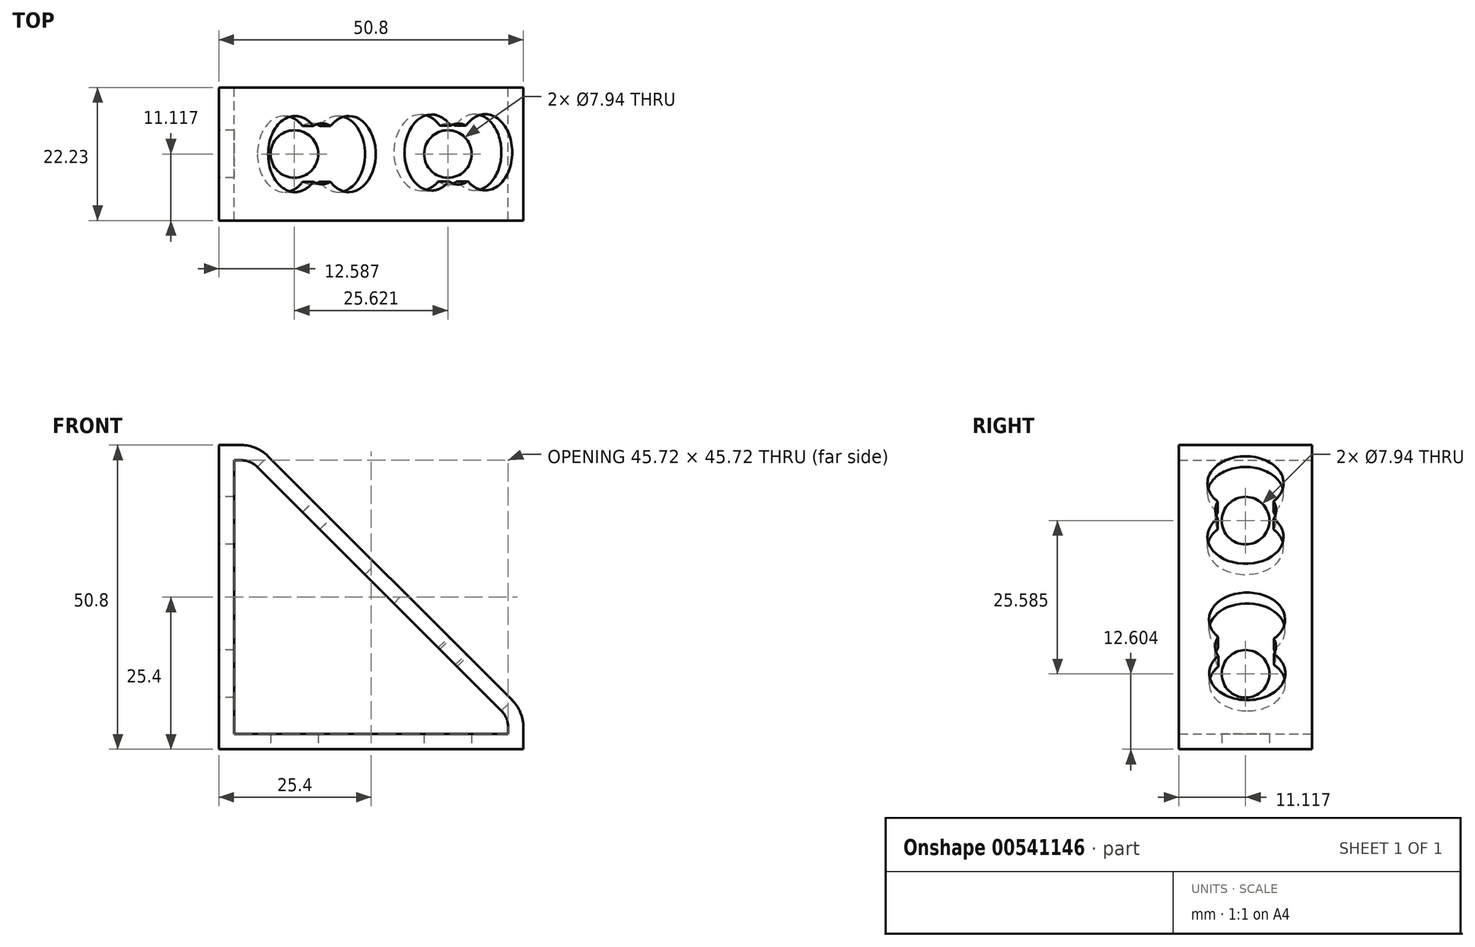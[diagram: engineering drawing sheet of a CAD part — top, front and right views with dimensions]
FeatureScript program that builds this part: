
annotation { "Feature Type Name" : "Feature", "Feature Type Description" : "" }
export const myFeature = defineFeature(function(context is Context, id is Id, definition is map)
    precondition{}
    {
        {
            var Q0;
            Q0=qCreatedBy(makeId("Front.planeOp"),FACE);
            var sketch = newSketch(context, id + "F0", { "sketchPlane" : qUnion([Q0])});
            skLineSegment(sketch, "E0", {"start": v(0, 0) * mm, "end": v(50.8, 0) * mm});
            skLineSegment(sketch, "E1", {"start": v(0, 0) * mm, "end": v(0, 50.8) * mm});
            skLineSegment(sketch, "E2", {"start": v(0, 50.8) * mm, "end": v(3.72, 50.8) * mm});
            skLineSegment(sketch, "E3", {"start": v(50.8, 0) * mm, "end": v(50.8, 3.72) * mm});
            skLineSegment(sketch, "E4", {"start": v(8.2, 48.94) * mm, "end": v(48.94, 8.2) * mm});
            skPoint(sketch, "E5.visualSharp", {"position": v(6.35, 50.8) * mm});
            skArc(sketch, "E5.filletArc", {"start": v(8.2, 48.94) * mm, "mid": v(6.15, 50.32) * mm, "end": v(3.72, 50.8) * mm});
            skPoint(sketch, "E6.visualSharp", {"position": v(50.8, 6.35) * mm});
            skArc(sketch, "E6.filletArc", {"start": v(50.8, 3.72) * mm, "mid": v(50.32, 6.15) * mm, "end": v(48.94, 8.2) * mm});
            skSolve(sketch);
        }
        {
            var Q0;
            Q0=makeQuery(id+"F0.imprint","IMPRINT",FACE,{"disambiguationData":[TD([[makeQuery(id+"F0.imprint","IMPRINT",EDGE,{"derivedFrom":sQuery(id+"F0.wireOp",EDGE,"E0")}),1.0]])]});
            extrude(context, id + "F1", {"entities" : qUnion([Q0]), "depth" : 22.22 * mm, "offsetDistance" : 25.4 * mm});
        }
        {
            var Q0;
            Q0=makeQuery(id+"F1.opExtrude","CAP_FACE",FACE,{"disambiguationData":[OSD([sQuery(id+"F0.wireOp",EDGE,"E0"),sQuery(id+"F0.wireOp",EDGE,"E1"),sQuery(id+"F0.wireOp",EDGE,"E2"),sQuery(id+"F0.wireOp",EDGE,"E3"),sQuery(id+"F0.wireOp",EDGE,"E4")])],"isStart":false});
            var Q1;
            Q1=makeQuery(id+"F1.opExtrude","CAP_FACE",FACE,{"disambiguationData":[OSD([sQuery(id+"F0.wireOp",EDGE,"E0"),sQuery(id+"F0.wireOp",EDGE,"E1"),sQuery(id+"F0.wireOp",EDGE,"E2"),sQuery(id+"F0.wireOp",EDGE,"E3"),sQuery(id+"F0.wireOp",EDGE,"E4")])],"isStart":true});
            shell(context, id + "F2", {"entities" : qUnion([Q0, Q1]), "thickness" : 2.54 * mm});
        }
        {
            var Q0;
            Q0=makeQuery(id+"F1.opExtrude","SWEPT_FACE",FACE,{"disambiguationData":[OSD([sQuery(id+"F0.wireOp",EDGE,"E0")])]});
            var sketch = newSketch(context, id + "F3", { "sketchPlane" : qUnion([Q0])});
            skPoint(sketch, "E7.second.point", {"position": v(34.93, 11.11) * mm});
            skPoint(sketch, "E7.third.point", {"position": v(35.12, 9.96) * mm});
            skPoint(sketch, "E8.end.orphan", {"position": v(42.86, 11.11) * mm});
            skPoint(sketch, "E8.start.orphan", {"position": v(50.8, 11.11) * mm});
            skPoint(sketch, "E9.second.point", {"position": v(15.86, 11.11) * mm});
            skPoint(sketch, "E9.third.point", {"position": v(15.84, 10.35) * mm});
            skPoint(sketch, "E10.end.orphan", {"position": v(7.94, 11.11) * mm});
            skPoint(sketch, "E10.start.orphan", {"position": v(0, 11.11) * mm});
            skLineSegment(sketch, "E11", {"start": v(0, 11.11) * mm, "end": v(12.59, 11.11) * mm});
            skLineSegment(sketch, "E12", {"start": v(50.8, 11.11) * mm, "end": v(38.2, 11.11) * mm});
            skCircle(sketch, "E13", {"center": v(12.59, 11.11) * mm, "radius": 3.97 * mm});
            skCircle(sketch, "E14", {"center": v(38.2, 11.11) * mm, "radius": 3.97 * mm});
            skSolve(sketch);
        }
        {
            var Q0;
            Q0=makeQuery(id+"F1.opExtrude","SWEPT_FACE",FACE,{"disambiguationData":[OSD([sQuery(id+"F0.wireOp",EDGE,"E1")])]});
            var sketch = newSketch(context, id + "F4", { "sketchPlane" : qUnion([Q0])});
            skPoint(sketch, "E15.second.point", {"position": v(11.11, 36.27) * mm});
            skPoint(sketch, "E15.third.point", {"position": v(9.6, 36.55) * mm});
            skPoint(sketch, "E16.end.orphan", {"position": v(11.11, 42.86) * mm});
            skPoint(sketch, "E16.start.orphan", {"position": v(11.11, 50.8) * mm});
            skLineSegment(sketch, "E17", {"start": v(11.11, 50.8) * mm, "end": v(11.11, 38.19) * mm});
            skLineSegment(sketch, "E18", {"start": v(11.11, 0) * mm, "end": v(11.11, 12.6) * mm});
            skCircle(sketch, "E19", {"center": v(11.11, 38.19) * mm, "radius": 3.97 * mm});
            skCircle(sketch, "E20", {"center": v(11.11, 12.6) * mm, "radius": 3.97 * mm});
            skSolve(sketch);
        }
        {
            var Q0;
            Q0=sQuery(id+"F3.wireOp",VERTEX,"E13.center");
            var Q1;
            Q1=makeQuery(id+"F1.opExtrude","SWEPT_BODY",BODY,{"disambiguationData":[OSD([sQuery(id+"F0.wireOp",EDGE,"E0"),sQuery(id+"F0.wireOp",EDGE,"E1"),sQuery(id+"F0.wireOp",EDGE,"E2"),sQuery(id+"F0.wireOp",EDGE,"E3"),sQuery(id+"F0.wireOp",EDGE,"E4")])]});
            hole(context, id + "F5", {"style" : HoleStyle.SIMPLE, "endStyle" : HoleEndStyle.BLIND, "holeDiameter" : 7.94 * mm, "holeDepth" : 2.54 * mm, "isTappedThrough" : true, "tappedDepth" : 12.7 * mm, "tapClearance" : 3, "locations" : qUnion([Q0]), "scope" : qUnion([Q1])});
        }
        {
            var Q0;
            Q0=sQuery(id+"F3.wireOp",VERTEX,"E14.center");
            var Q1;
            Q1=makeQuery(id+"F1.opExtrude","SWEPT_BODY",BODY,{"disambiguationData":[OSD([sQuery(id+"F0.wireOp",EDGE,"E0"),sQuery(id+"F0.wireOp",EDGE,"E1"),sQuery(id+"F0.wireOp",EDGE,"E2"),sQuery(id+"F0.wireOp",EDGE,"E3"),sQuery(id+"F0.wireOp",EDGE,"E4")])]});
            hole(context, id + "F6", {"style" : HoleStyle.SIMPLE, "endStyle" : HoleEndStyle.BLIND, "holeDiameter" : 7.94 * mm, "holeDepth" : 2.54 * mm, "isTappedThrough" : true, "tappedDepth" : 12.7 * mm, "tapClearance" : 3, "locations" : qUnion([Q0]), "scope" : qUnion([Q1])});
        }
        {
            var Q0;
            Q0=sQuery(id+"F4.wireOp",VERTEX,"E19.center");
            var Q1;
            Q1=sQuery(id+"F4.wireOp",VERTEX,"E20.center");
            var Q2;
            Q2=makeQuery(id+"F1.opExtrude","SWEPT_BODY",BODY,{"disambiguationData":[OSD([sQuery(id+"F0.wireOp",EDGE,"E0"),sQuery(id+"F0.wireOp",EDGE,"E1"),sQuery(id+"F0.wireOp",EDGE,"E2"),sQuery(id+"F0.wireOp",EDGE,"E3"),sQuery(id+"F0.wireOp",EDGE,"E4")])]});
            hole(context, id + "F7", {"style" : HoleStyle.SIMPLE, "endStyle" : HoleEndStyle.BLIND, "holeDiameter" : 7.94 * mm, "holeDepth" : 2.54 * mm, "isTappedThrough" : true, "tappedDepth" : 12.7 * mm, "tapClearance" : 3, "locations" : qUnion([Q0, Q1]), "scope" : qUnion([Q2])});
        }
        {
            var Q0;
            Q0=makeQuery(id+"F1.opExtrude","SWEPT_FACE",FACE,{"disambiguationData":[OSD([sQuery(id+"F0.wireOp",EDGE,"E4")])]});
            var sketch = newSketch(context, id + "F8", { "sketchPlane" : qUnion([Q0])});
            skLineSegment(sketch, "E21", {"start": v(-11.11, 28.8) * mm, "end": v(-11.11, 16.1) * mm});
            skLineSegment(sketch, "E22", {"start": v(-11.11, 16.1) * mm, "end": v(-11.11, 3.4) * mm});
            skArc(sketch, "E23", {"start": v(-6.73, 17.86) * mm, "mid": v(-5.22, 24.81) * mm, "end": v(-11.11, 28.8) * mm});
            skArc(sketch, "E24", {"start": v(-11.11, 3.4) * mm, "mid": v(-5.21, 7.4) * mm, "end": v(-6.74, 14.36) * mm});
            skArc(sketch, "E25", {"start": v(-11.11, 28.8) * mm, "mid": v(-16.96, 24.93) * mm, "end": v(-15.68, 18.04) * mm});
            skArc(sketch, "E26", {"start": v(-15.68, 14.16) * mm, "mid": v(-16.96, 7.27) * mm, "end": v(-11.11, 3.4) * mm});
            skArc(sketch, "E27", {"start": v(-15.68, 18.04) * mm, "mid": v(-16.08, 16.1) * mm, "end": v(-15.68, 14.16) * mm});
            skArc(sketch, "E28", {"start": v(-6.74, 14.36) * mm, "mid": v(-6.4, 16.1) * mm, "end": v(-6.73, 17.86) * mm});
            skLineSegment(sketch, "E29", {"start": v(-11.11, -28.8) * mm, "end": v(-11.11, -16.1) * mm});
            skLineSegment(sketch, "E30", {"start": v(-11.11, -16.1) * mm, "end": v(-11.11, -3.4) * mm});
            skArc(sketch, "E31", {"start": v(-15.12, -17.77) * mm, "mid": v(-16.8, -24.62) * mm, "end": v(-11.11, -28.8) * mm});
            skArc(sketch, "E32", {"start": v(-11.11, -28.8) * mm, "mid": v(-5.2, -25.2) * mm, "end": v(-6.1, -18.32) * mm});
            skArc(sketch, "E33", {"start": v(-11.11, -16.1) * mm, "mid": v(-10.9, -16.1) * mm, "end": v(-10.68, -16.1) * mm});
            skArc(sketch, "E34", {"start": v(-11.11, -3.4) * mm, "mid": v(-16.91, -7.57) * mm, "end": v(-15.17, -14.5) * mm});
            skArc(sketch, "E35", {"start": v(-6.1, -18.32) * mm, "mid": v(-5.8, -16.24) * mm, "end": v(-6.33, -14.2) * mm});
            skArc(sketch, "E36", {"start": v(-15.17, -14.5) * mm, "mid": v(-15.47, -16.14) * mm, "end": v(-15.12, -17.77) * mm});
            skArc(sketch, "E37.trimOffspring", {"start": v(-10.68, -16.1) * mm, "mid": v(-10.9, -16.1) * mm, "end": v(-11.11, -16.1) * mm});
            skArc(sketch, "E38.trimOffspring", {"start": v(-6.33, -14.2) * mm, "mid": v(-5.05, -7.18) * mm, "end": v(-11.11, -3.4) * mm});
            skSolve(sketch);
        }
        {
            var Q0;
            Q0=sQuery(id+"F8.wireOp",VERTEX,"E23.center");
            var Q1;
            Q1=makeQuery(id+"F1.opExtrude","SWEPT_BODY",BODY,{"disambiguationData":[OSD([sQuery(id+"F0.wireOp",EDGE,"E0"),sQuery(id+"F0.wireOp",EDGE,"E1"),sQuery(id+"F0.wireOp",EDGE,"E2"),sQuery(id+"F0.wireOp",EDGE,"E3"),sQuery(id+"F0.wireOp",EDGE,"E4"),sQuery(id+"F0.wireOp",EDGE,"E5.filletArc"),sQuery(id+"F0.wireOp",EDGE,"E6.filletArc")])]});
            hole(context, id + "F9", {"style" : HoleStyle.SIMPLE, "endStyle" : HoleEndStyle.BLIND, "holeDiameter" : 12.7 * mm, "holeDepth" : 2.54 * mm, "isTappedThrough" : true, "tappedDepth" : 12.7 * mm, "tapClearance" : 3, "locations" : qUnion([Q0]), "scope" : qUnion([Q1])});
        }
        {
            var Q0;
            Q0=sQuery(id+"F8.wireOp",VERTEX,"E27.center");
            var Q1;
            Q1=makeQuery(id+"F1.opExtrude","SWEPT_BODY",BODY,{"disambiguationData":[OSD([sQuery(id+"F0.wireOp",EDGE,"E0"),sQuery(id+"F0.wireOp",EDGE,"E1"),sQuery(id+"F0.wireOp",EDGE,"E2"),sQuery(id+"F0.wireOp",EDGE,"E3"),sQuery(id+"F0.wireOp",EDGE,"E4"),sQuery(id+"F0.wireOp",EDGE,"E5.filletArc"),sQuery(id+"F0.wireOp",EDGE,"E6.filletArc")])]});
            hole(context, id + "F10", {"style" : HoleStyle.SIMPLE, "endStyle" : HoleEndStyle.BLIND, "holeDiameter" : 10.16 * mm, "holeDepth" : 2.54 * mm, "isTappedThrough" : true, "tappedDepth" : 12.7 * mm, "tapClearance" : 3, "locations" : qUnion([Q0]), "scope" : qUnion([Q1])});
        }
        {
            var Q0;
            Q0=sQuery(id+"F8.wireOp",VERTEX,"E24.center");
            var Q1;
            Q1=makeQuery(id+"F1.opExtrude","SWEPT_BODY",BODY,{"disambiguationData":[OSD([sQuery(id+"F0.wireOp",EDGE,"E0"),sQuery(id+"F0.wireOp",EDGE,"E1"),sQuery(id+"F0.wireOp",EDGE,"E2"),sQuery(id+"F0.wireOp",EDGE,"E3"),sQuery(id+"F0.wireOp",EDGE,"E4"),sQuery(id+"F0.wireOp",EDGE,"E5.filletArc"),sQuery(id+"F0.wireOp",EDGE,"E6.filletArc")])]});
            hole(context, id + "F11", {"style" : HoleStyle.SIMPLE, "endStyle" : HoleEndStyle.BLIND, "holeDiameter" : 12.7 * mm, "holeDepth" : 2.54 * mm, "isTappedThrough" : true, "tappedDepth" : 12.7 * mm, "tapClearance" : 3, "locations" : qUnion([Q0]), "scope" : qUnion([Q1])});
        }
        {
            var Q0;
            Q0=sQuery(id+"F8.wireOp",VERTEX,"E33.center");
            var Q1;
            Q1=makeQuery(id+"F1.opExtrude","SWEPT_BODY",BODY,{"disambiguationData":[OSD([sQuery(id+"F0.wireOp",EDGE,"E0"),sQuery(id+"F0.wireOp",EDGE,"E1"),sQuery(id+"F0.wireOp",EDGE,"E2"),sQuery(id+"F0.wireOp",EDGE,"E3"),sQuery(id+"F0.wireOp",EDGE,"E4"),sQuery(id+"F0.wireOp",EDGE,"E5.filletArc"),sQuery(id+"F0.wireOp",EDGE,"E6.filletArc")])]});
            hole(context, id + "F12", {"style" : HoleStyle.SIMPLE, "endStyle" : HoleEndStyle.BLIND, "holeDiameter" : 12.7 * mm, "holeDepth" : 2.54 * mm, "isTappedThrough" : true, "tappedDepth" : 12.7 * mm, "tapClearance" : 3, "locations" : qUnion([Q0]), "scope" : qUnion([Q1])});
        }
        {
            var Q0;
            Q0=sQuery(id+"F8.wireOp",VERTEX,"E29.end");
            var Q1;
            Q1=makeQuery(id+"F1.opExtrude","SWEPT_BODY",BODY,{"disambiguationData":[OSD([sQuery(id+"F0.wireOp",EDGE,"E0"),sQuery(id+"F0.wireOp",EDGE,"E1"),sQuery(id+"F0.wireOp",EDGE,"E2"),sQuery(id+"F0.wireOp",EDGE,"E3"),sQuery(id+"F0.wireOp",EDGE,"E4"),sQuery(id+"F0.wireOp",EDGE,"E5.filletArc"),sQuery(id+"F0.wireOp",EDGE,"E6.filletArc")])]});
            hole(context, id + "F13", {"style" : HoleStyle.SIMPLE, "endStyle" : HoleEndStyle.BLIND, "holeDiameter" : 10.16 * mm, "holeDepth" : 2.54 * mm, "isTappedThrough" : true, "tappedDepth" : 12.7 * mm, "tapClearance" : 3, "locations" : qUnion([Q0]), "scope" : qUnion([Q1])});
        }
        {
            var Q0;
            Q0=sQuery(id+"F8.wireOp",VERTEX,"E31.center");
            var Q1;
            Q1=makeQuery(id+"F1.opExtrude","SWEPT_BODY",BODY,{"disambiguationData":[OSD([sQuery(id+"F0.wireOp",EDGE,"E0"),sQuery(id+"F0.wireOp",EDGE,"E1"),sQuery(id+"F0.wireOp",EDGE,"E2"),sQuery(id+"F0.wireOp",EDGE,"E3"),sQuery(id+"F0.wireOp",EDGE,"E4"),sQuery(id+"F0.wireOp",EDGE,"E5.filletArc"),sQuery(id+"F0.wireOp",EDGE,"E6.filletArc")])]});
            hole(context, id + "F14", {"style" : HoleStyle.SIMPLE, "endStyle" : HoleEndStyle.BLIND, "holeDiameter" : 12.7 * mm, "holeDepth" : 2.54 * mm, "isTappedThrough" : true, "tappedDepth" : 12.7 * mm, "tapClearance" : 3, "locations" : qUnion([Q0]), "scope" : qUnion([Q1])});
        }
    });
